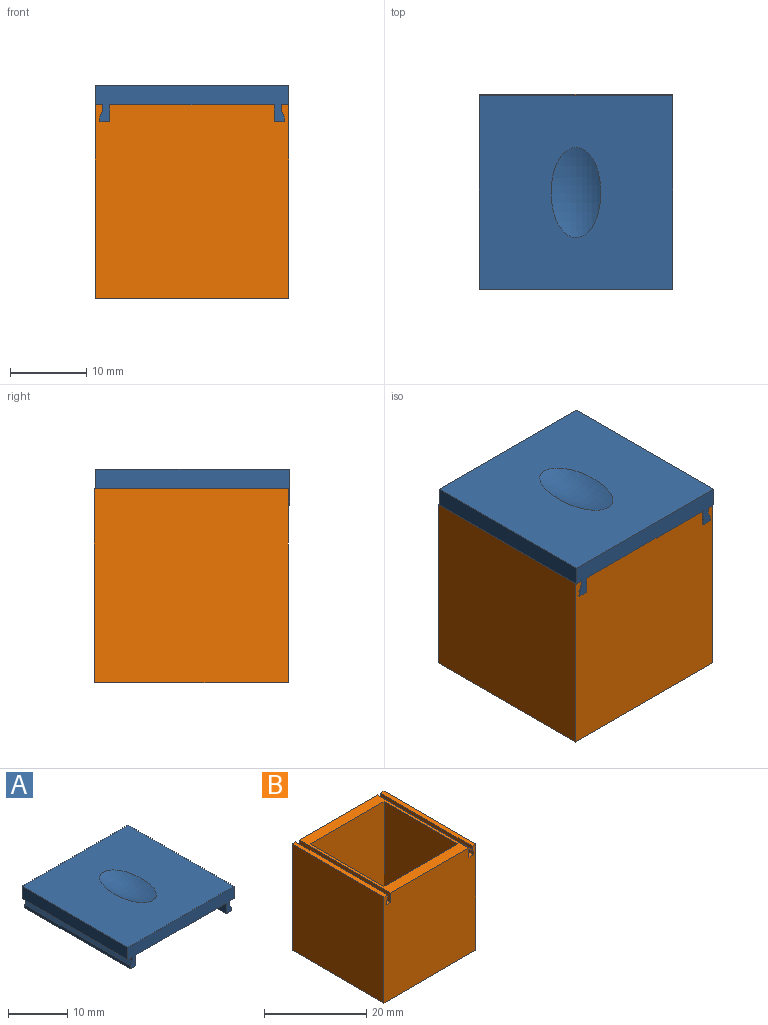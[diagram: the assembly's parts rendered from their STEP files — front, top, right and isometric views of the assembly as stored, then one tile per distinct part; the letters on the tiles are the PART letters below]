
ASSEMBLY  parts=2 mates=1
PART A: 19 faces, bbox 25.4x25.4x6.4 mm
  f0: plane 25.4x25.4mm, normal (0,0,1), area 584.5mm2, adj f3,f4,f5,f6,f18
  f1: plane 25.4x21.59mm, normal (0,0,-1), area 548.4mm2, adj f4,f6,f12,f14
  f2: plane 25.4x1.02mm, normal (0,0,-1), area 25.8mm2, adj f4,f5,f6,f8
  f3: plane 25.4x2.54mm, normal (1,0,0), area 64.5mm2, adj f0,f4,f6,f7
  f4: plane 25.4x4.76mm, normal (0,1,0), area 69.3mm2, adj f0,f1,f2,f3,f5,f7,f8,f9
  f5: plane 25.4x2.54mm, normal (-1,0,0), area 64.5mm2, adj f0,f2,f4,f6
  f6: plane 25.4x4.76mm, normal (0,-1,0), area 69.3mm2, adj f0,f1,f2,f3,f5,f7,f8,f9
  f7: plane 25.4x1.02mm, normal (0,0,-1), area 25.8mm2, adj f3,f4,f6,f13
  f8: plane 25.4x0.79mm, normal (-1,0,0), area 20.2mm2, adj f2,f4,f6,f9
  f9: plane 25.4x0.79mm, normal (-0.9,0,0.43), area 22.4mm2, adj f4,f6,f8,f10
  f10: plane 25.4x0.64mm, normal (-1,0,0), area 16.1mm2, adj f4,f6,f9,f11
  f11: plane 25.4x1.27mm, normal (0,0,-1), area 32.3mm2, adj f4,f6,f10,f12
  f12: plane 25.4x2.22mm, normal (1,0,0), area 56.5mm2, adj f1,f4,f6,f11
  f13: plane 25.4x0.79mm, normal (1,0,0), area 20.2mm2, adj f4,f6,f7,f17
  f14: plane 25.4x2.22mm, normal (-1,0,0), area 56.5mm2, adj f1,f4,f6,f15
  f15: plane 25.4x1.27mm, normal (0,0,-1), area 32.3mm2, adj f4,f6,f14,f16
  f16: plane 25.4x0.64mm, normal (1,0,0), area 16.1mm2, adj f4,f6,f15,f17
  f17: plane 25.4x0.79mm, normal (0.9,0,0.43), area 22.4mm2, adj f4,f6,f13,f16
  f18: torus R=12.69mm, axis (1,0,0), area 64.2mm2, adj f0
PART B: 23 faces, bbox 25.4x25.4x25.4 mm
  f0: plane 25.4x21.59mm, normal (0,0,1), area 135.5mm2, adj f2,f3,f8,f10,f11,f12,f14,f22
  f1: plane 25.4x1.02mm, normal (0,0,1), area 25.8mm2, adj f2,f3,f7,f13
  f2: plane 25.4x25.4mm, normal (0,1,0), area 640.4mm2, adj f0,f1,f4,f5,f6,f7,f13,f14
  f3: plane 25.4x25.4mm, normal (0,-1,0), area 640.4mm2, adj f0,f1,f4,f5,f6,f7,f13,f14
  f4: plane 25.4x1.02mm, normal (0,0,1), area 25.8mm2, adj f2,f3,f5,f18
  f5: plane 25.4x25.4mm, normal (-1,0,0), area 645.2mm2, adj f2,f3,f4,f6
  f6: plane 25.4x25.4mm, normal (0,0,-1), area 645.2mm2, adj f2,f3,f5,f7
  f7: plane 25.4x25.4mm, normal (1,0,0), area 645.2mm2, adj f1,f2,f3,f6
  f8: plane 22.86x20.32mm, normal (1,0,0), area 464.5mm2, adj f0,f9,f11,f12
  f9: plane 20.32x20.32mm, normal (0,0,1), area 412.9mm2, adj f8,f10,f11,f12
  f10: plane 22.86x20.32mm, normal (-1,0,0), area 464.5mm2, adj f0,f9,f11,f12
  f11: plane 22.86x20.32mm, normal (0,-1,0), area 464.5mm2, adj f0,f8,f9,f10
  f12: plane 22.86x20.32mm, normal (0,1,0), area 464.5mm2, adj f0,f8,f9,f10
  f13: plane 25.4x0.79mm, normal (-1,0,0), area 20.2mm2, adj f1,f2,f3,f17
  f14: plane 25.4x2.22mm, normal (1,0,0), area 56.5mm2, adj f0,f2,f3,f15
  f15: plane 25.4x1.27mm, normal (0,0,1), area 32.3mm2, adj f2,f3,f14,f16
  f16: plane 25.4x0.64mm, normal (-1,0,0), area 16.1mm2, adj f2,f3,f15,f17
  f17: plane 25.4x0.79mm, normal (-0.9,0,-0.43), area 22.4mm2, adj f2,f3,f13,f16
  f18: plane 25.4x0.79mm, normal (1,0,0), area 20.2mm2, adj f2,f3,f4,f19
  f19: plane 25.4x0.79mm, normal (0.9,0,-0.43), area 22.4mm2, adj f2,f3,f18,f20
  f20: plane 25.4x0.64mm, normal (1,0,0), area 16.1mm2, adj f2,f3,f19,f21
  f21: plane 25.4x1.27mm, normal (0,0,1), area 32.3mm2, adj f2,f3,f20,f22
  f22: plane 25.4x2.22mm, normal (-1,0,0), area 56.5mm2, adj f0,f2,f3,f21
PLACE A t=(-1.16,-3.99,8)mm
PLACE B t=(-1.16,-16.55,-4.7)mm fixed
MATE slider A.f6 <-> B.f3  axis (0,-1,0) through (-12.59,-16.69,5.78)mm
